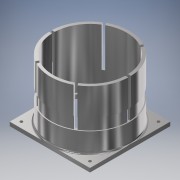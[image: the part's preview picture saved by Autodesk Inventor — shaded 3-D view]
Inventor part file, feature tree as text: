
AUTODESK INVENTOR PART (.ipt)
format: ipt  version: 2016 (Build 200138000, 138)  size: 230,400 bytes
history: native  units: mm
features: sketch x6, extrude x5, pattern_circular x1, hole x1, fillet x1, reference x1, projected_geometry x1
ambient origin geometry x8: Origin, YZ Plane, XZ Plane, XY Plane, X Axis, Y Axis, Z Axis, Center Point
bodies: Solid1 (feature_tree)
feature tree (16):
  extrude  "Extrusion1"  Depth=60.0mm TaperAngle=0.0deg
  extrude  "Extrusion9"  Depth=12.0mm TaperAngle=0.0deg
  pattern_circular  "Circular Pattern2"  Count=4  [1 undecoded]
  extrude  "Extrusion10"  Depth=60.0mm
  extrude  "Extrusion11"  Depth=82.0mm
  hole  "Hole1"  [1 undecoded]
  fillet  "Fillet2"  Radius=4.0mm
  extrude  "Extrusion8"  Depth=2.0mm
  sketch  "Sketch1"  dims[d0=3.0mm d1=60.0mm d2=0.0mm]
  reference  "Reference1"
  sketch  "Sketch7"  dims[d27=1.0mm d28=12.0mm d29=0.0mm]
  sketch  "Sketch8"  dims[d30=0.698132mm d31=40.0mm d32=0.0mm]
  sketch  "Sketch9"  dims[d33=60.0mm d34=360.0deg d36=1.0mm]
  projected_geometry  "Projected Loop4"
  sketch  "Sketch10"  dims[d37=12.0mm d38=0.0mm d39=82.0mm]
  sketch  "Sketch11"  dims[d40=82.0mm d41=2.0mm d42=4.0mm d43=0.0mm d44=6.0mm d45=3.0mm d46=6.0mm d47=4.0mm d48=2.0mm d49=90.0deg d50=8.0mm d51=20.594885mm d52=2.0mm]
note: 2 required parameter values undecoded (feature->parameter linkage not recoverable at this tier; creation-order binding heuristic only, values carry confidence <= 0.55)
